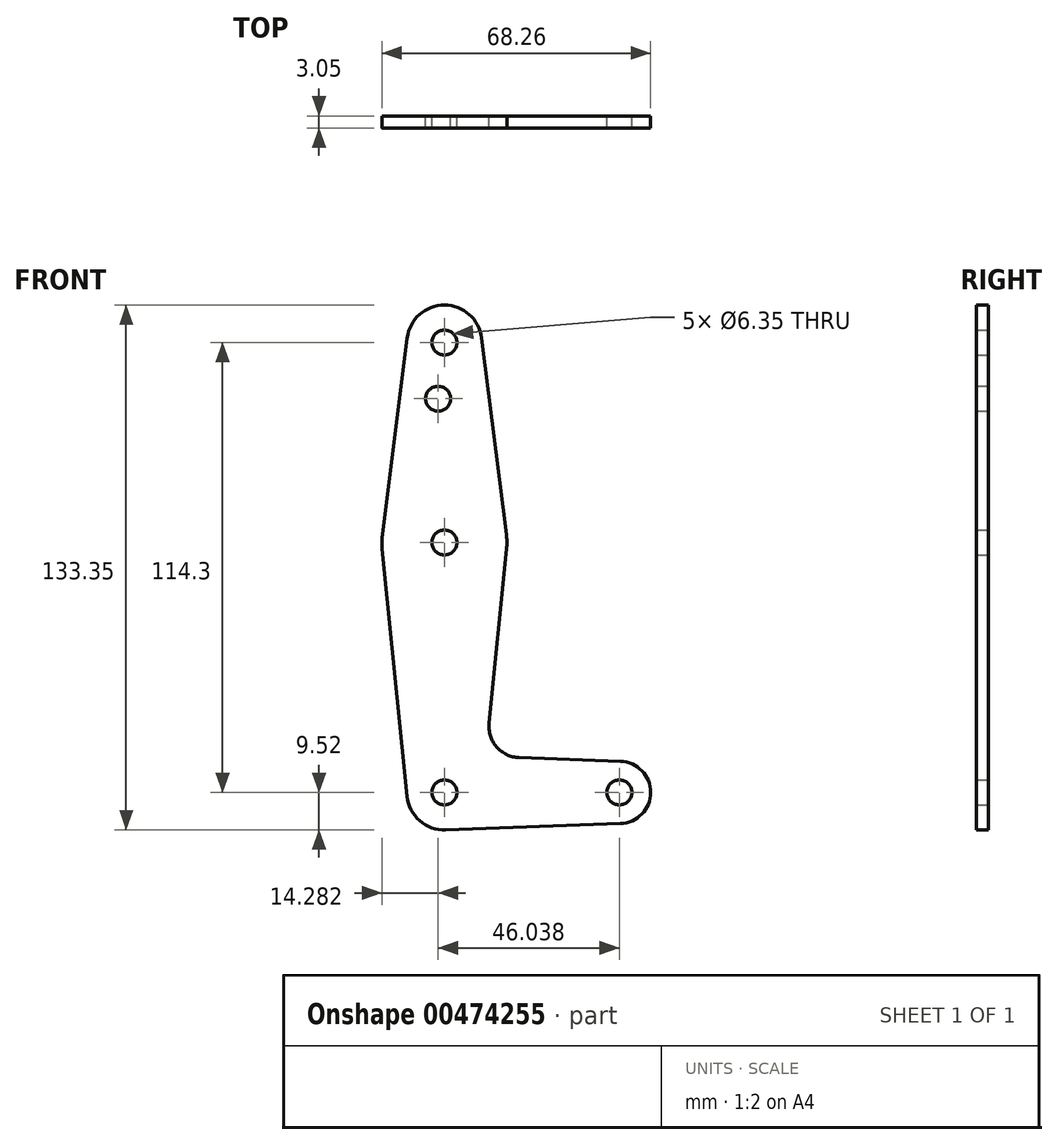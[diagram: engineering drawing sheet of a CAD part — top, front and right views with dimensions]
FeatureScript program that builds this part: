
annotation { "Feature Type Name" : "Feature", "Feature Type Description" : "" }
export const myFeature = defineFeature(function(context is Context, id is Id, definition is map)
    precondition{}
    {
        {
            var Q0;
            Q0=qCreatedBy(makeId("Front.planeOp"),FACE);
            var sketch = newSketch(context, id + "F0", { "sketchPlane" : qUnion([Q0])});
            skCircle(sketch, "E0", {"center": v(0, 0) * mm, "radius": 9.53 * mm});
            skCircle(sketch, "E1", {"center": v(0, 63.5) * mm, "radius": 15.88 * mm});
            skCircle(sketch, "E2", {"center": v(0, 114.3) * mm, "radius": 9.53 * mm});
            skCircle(sketch, "E3", {"center": v(44.45, 0) * mm, "radius": 7.94 * mm});
            skLineSegment(sketch, "E4", {"start": v(0, 0) * mm, "end": v(0, 114.3) * mm, "construction": true});
            skLineSegment(sketch, "E5", {"start": v(0, 0) * mm, "end": v(44.45, 0) * mm, "construction": true});
            skLineSegment(sketch, "E6", {"start": v(-15.75, 65.48) * mm, "end": v(-9.45, 115.5) * mm});
            skLineSegment(sketch, "E7", {"start": v(-15.8, 61.91) * mm, "end": v(-9.48, -0.95) * mm});
            skLineSegment(sketch, "E8", {"start": v(11.34, 17.6) * mm, "end": v(15.8, 61.91) * mm});
            skLineSegment(sketch, "E9", {"start": v(18.97, 8.85) * mm, "end": v(44.73, 7.93) * mm});
            skLineSegment(sketch, "E10", {"start": v(0.34, -9.52) * mm, "end": v(44.73, -7.93) * mm});
            skLineSegment(sketch, "E11", {"start": v(9.45, 115.5) * mm, "end": v(15.75, 65.48) * mm});
            skCircle(sketch, "E12", {"center": v(0, 114.3) * mm, "radius": 3.18 * mm});
            skCircle(sketch, "E13", {"center": v(0, 63.5) * mm, "radius": 3.18 * mm});
            skCircle(sketch, "E14", {"center": v(-1.59, 100.03) * mm, "radius": 3.18 * mm});
            skCircle(sketch, "E15", {"center": v(0, 0) * mm, "radius": 3.18 * mm});
            skCircle(sketch, "E16", {"center": v(44.45, 0) * mm, "radius": 3.18 * mm});
            skArc(sketch, "E17.filletArc", {"start": v(11.34, 17.6) * mm, "mid": v(13.26, 11.57) * mm, "end": v(18.97, 8.85) * mm});
            skSolve(sketch);
        }
        {
            var Q0;
            Q0 = qSketchRegion(id + "F0", true);
            extrude(context, id + "F1", {"entities" : qUnion([Q0]), "depth" : 3.05 * mm});
        }
    });
